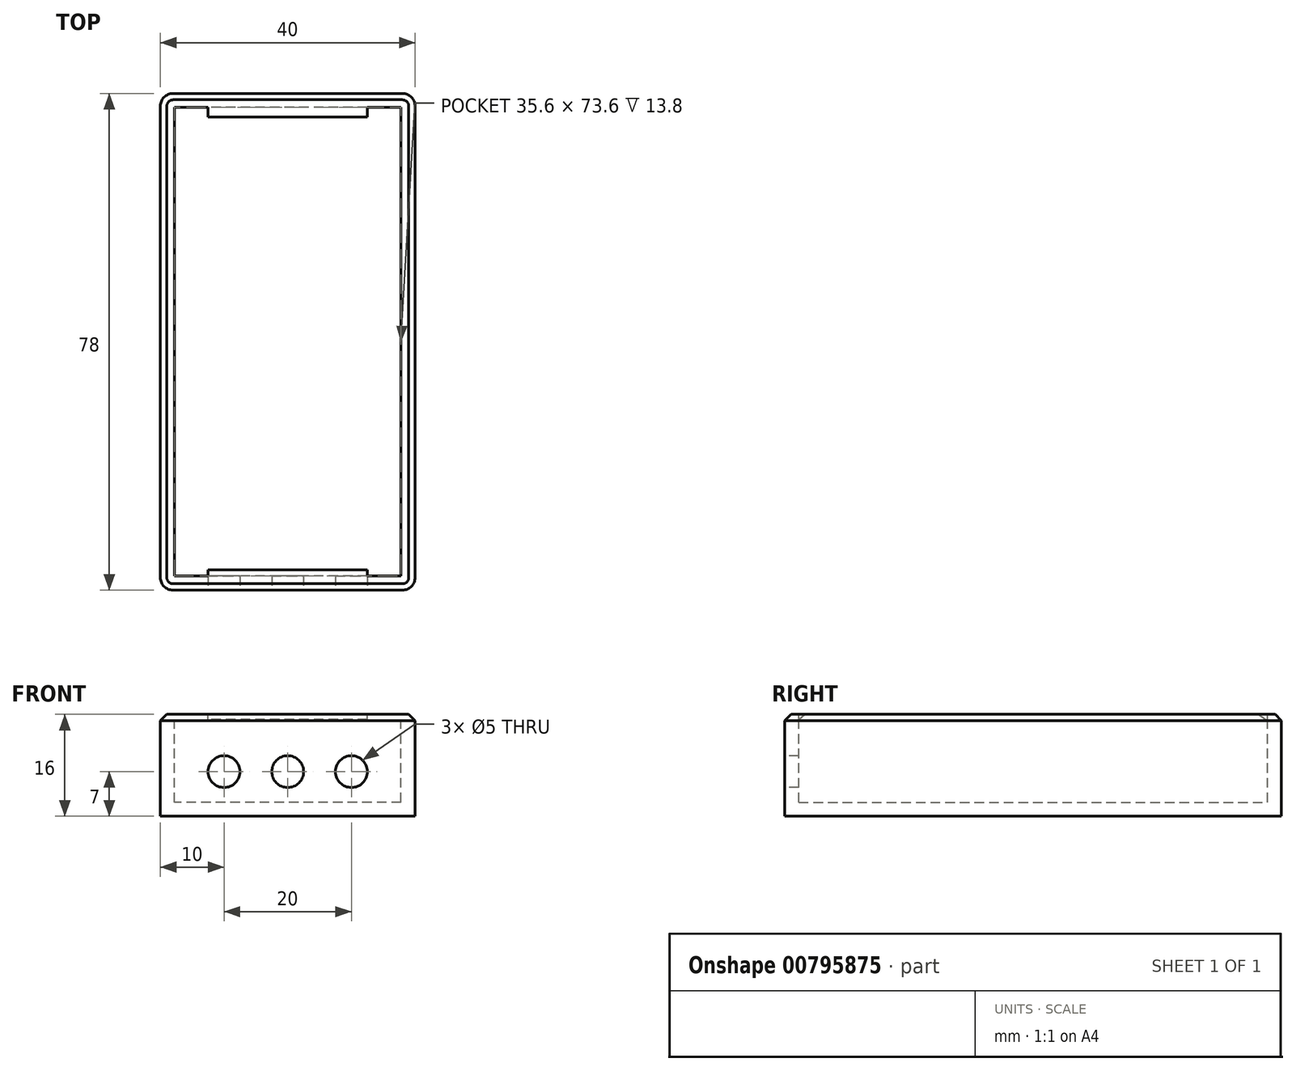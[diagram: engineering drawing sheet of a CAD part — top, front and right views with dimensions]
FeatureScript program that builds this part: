
annotation { "Feature Type Name" : "Feature", "Feature Type Description" : "" }
export const myFeature = defineFeature(function(context is Context, id is Id, definition is map)
    precondition{}
    {
        {
            var Q0;
            Q0=qCreatedBy(makeId("Top.planeOp"),FACE);
            var sketch = newSketch(context, id + "F0", { "sketchPlane" : qUnion([Q0])});
            skLineSegment(sketch, "E0.bottom", {"start": v(20, -39) * mm, "end": v(-20, -39) * mm});
            skLineSegment(sketch, "E0.top", {"start": v(20, 39) * mm, "end": v(-20, 39) * mm});
            skLineSegment(sketch, "E0.left", {"start": v(20, -39) * mm, "end": v(20, 39) * mm});
            skLineSegment(sketch, "E0.right", {"start": v(-20, -39) * mm, "end": v(-20, 39) * mm});
            skSolve(sketch);
        }
        {
            var Q0;
            Q0 = qSketchRegion(id + "F0", true);
            extrude(context, id + "F1", {"entities" : qUnion([Q0]), "depth" : 16 * mm, "offsetDistance" : 25 * mm});
        }
        {
            var Q0;
            Q0=makeQuery(id+"F1.opExtrude","SWEPT_EDGE",EDGE,{"disambiguationData":[OSD([sQuery(id+"F0.wireOp",EDGE,"E0.bottom"),sQuery(id+"F0.wireOp",EDGE,"E0.right")])]});
            var Q1;
            Q1=makeQuery(id+"F1.opExtrude","SWEPT_EDGE",EDGE,{"disambiguationData":[OSD([sQuery(id+"F0.wireOp",EDGE,"E0.bottom"),sQuery(id+"F0.wireOp",EDGE,"E0.left")])]});
            var Q2;
            Q2=makeQuery(id+"F1.opExtrude","SWEPT_EDGE",EDGE,{"disambiguationData":[OSD([sQuery(id+"F0.wireOp",EDGE,"E0.top"),sQuery(id+"F0.wireOp",EDGE,"E0.right")])]});
            var Q3;
            Q3=makeQuery(id+"F1.opExtrude","SWEPT_EDGE",EDGE,{"disambiguationData":[OSD([sQuery(id+"F0.wireOp",EDGE,"E0.top"),sQuery(id+"F0.wireOp",EDGE,"E0.left")])]});
            fillet(context, id + "F2", {"entities" : qUnion([Q0, Q1, Q2, Q3]), "radius" : 2 * mm, "tangentPropagation" : true, "allowEdgeOverflow" : false});
        }
        {
            var Q0;
            Q0=makeQuery(id+"F1.opExtrude","CAP_FACE",FACE,{"disambiguationData":[OSD([sQuery(id+"F0.wireOp",EDGE,"E0.bottom"),sQuery(id+"F0.wireOp",EDGE,"E0.top"),sQuery(id+"F0.wireOp",EDGE,"E0.left"),sQuery(id+"F0.wireOp",EDGE,"E0.right")])],"isStart":false});
            shell(context, id + "F3", {"entities" : qUnion([Q0]), "thickness" : 2.2 * mm});
        }
        {
            var Q0;
            Q0=makeQuery(id+"F1.opExtrude","SWEPT_FACE",FACE,{"disambiguationData":[OSD([sQuery(id+"F0.wireOp",EDGE,"E0.bottom")])]});
            var sketch = newSketch(context, id + "F4", { "sketchPlane" : qUnion([Q0])});
            skCircle(sketch, "E1", {"center": v(-10, 7) * mm, "radius": 2.5 * mm});
            skLineSegment(sketch, "E2", {"start": v(-10, 7) * mm, "end": v(0, 7) * mm, "construction": true});
            skCircle(sketch, "E3", {"center": v(0, 7) * mm, "radius": 2.5 * mm});
            skCircle(sketch, "E4.MirrorC", {"center": v(10, 7) * mm, "radius": 2.5 * mm});
            skSolve(sketch);
        }
        {
            var Q0;
            Q0 = qSketchRegion(id + "F4", true);
            var Q1;
            Q1=makeQuery(id+"F3.opShell","OFFSET_FACE",FACE,{"disambiguationData":[OSD([sQuery(id+"F0.wireOp",EDGE,"E0.bottom")])]});
            extrude(context, id + "F5", {"entities" : qUnion([Q0]), "operationType" : NewBodyOperationType.REMOVE, "endBound" : BoundingType.UP_TO_SURFACE, "oppositeDirection" : true, "depth" : 25 * mm, "endBoundEntityFace" : qUnion([Q1]), "offsetDistance" : 25 * mm});
        }
        {
            var Q0;
            Q0=qCreatedBy(makeId("Right.planeOp"),FACE);
            var sketch = newSketch(context, id + "F6", { "sketchPlane" : qUnion([Q0])});
            skLineSegment(sketch, "E5.0", {"start": v(-36.8, 15.16) * mm, "end": v(-36.8, 16) * mm});
            skLineSegment(sketch, "E6.0", {"start": v(-36.8, 16) * mm, "end": v(-35.8, 16) * mm});
            skLineSegment(sketch, "E7", {"start": v(-36.8, 15.16) * mm, "end": v(-35.8, 16) * mm});
            skLineSegment(sketch, "E8", {"start": v(-35.8, 16) * mm, "end": v(-36.8, 16) * mm});
            skLineSegment(sketch, "E9.0", {"start": v(36.8, 14.95) * mm, "end": v(36.8, 16) * mm});
            skLineSegment(sketch, "E10.0.2", {"start": v(36.8, 16) * mm, "end": v(35.3, 16) * mm});
            skLineSegment(sketch, "E11", {"start": v(36.8, 14.95) * mm, "end": v(35.3, 16) * mm});
            skLineSegment(sketch, "E12", {"start": v(35.3, 16) * mm, "end": v(36.8, 16) * mm});
            skPoint(sketch, "E10.0.1.start.orphan", {"position": v(37, 0) * mm});
            skPoint(sketch, "E13.orphan", {"position": v(37, 16) * mm});
            skPoint(sketch, "E14.orphan", {"position": v(36.8, 2.2) * mm});
            skPoint(sketch, "E15.orphan", {"position": v(-36.8, 2.2) * mm});
            skPoint(sketch, "E10.0.3.end.orphan", {"position": v(-37, 0) * mm});
            skPoint(sketch, "E16.orphan", {"position": v(-37, 16) * mm});
            skSolve(sketch);
        }
        {
            var Q0;
            Q0 = qSketchRegion(id + "F6", true);
            extrude(context, id + "F7", {"entities" : qUnion([Q0]), "operationType" : NewBodyOperationType.ADD, "endBound" : BoundingType.SYMMETRIC, "depth" : 25 * mm, "offsetDistance" : 25 * mm});
        }
        {
            var Q0;
            Q0=makeQuery(id+"F1.opExtrude","CAP_EDGE",EDGE,{"disambiguationData":[OSD([sQuery(id+"F0.wireOp",EDGE,"E0.bottom")])],"isStart":false});
            chamfer(context, id + "F8", {"entities" : qUnion([Q0]), "width" : 1 * mm, "tangentPropagation" : true});
        }
    });
